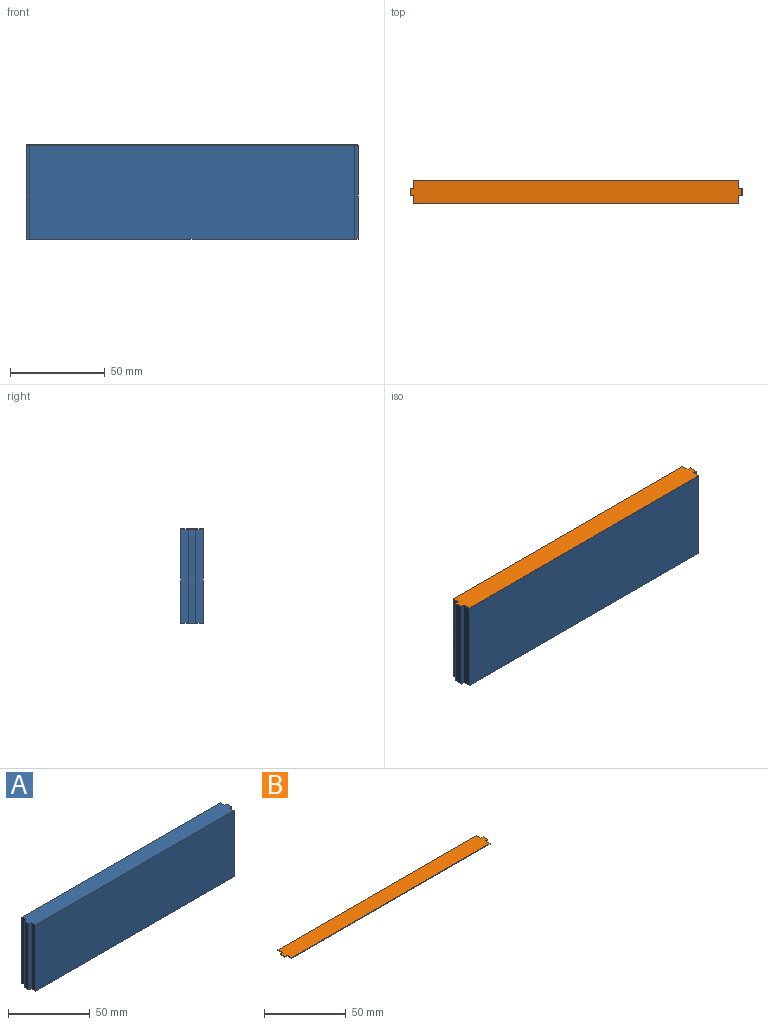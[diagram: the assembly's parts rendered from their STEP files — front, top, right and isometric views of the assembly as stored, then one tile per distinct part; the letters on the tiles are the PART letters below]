
ASSEMBLY  parts=2 mates=1
PART A: 14 faces, bbox 175x12x49.5 mm
  f0: plane 49.5x4mm, normal (-1,0,0), area 198mm2, adj f3,f4,f5,f8
  f1: plane 49.5x4mm, normal (-1,0,0), area 198mm2, adj f3,f5,f7,f8
  f2: plane 49.5x4mm, normal (-1,0,0), area 198mm2, adj f4,f5,f6,f8
  f3: plane 49.5x2mm, normal (0,1,0), area 99mm2, adj f0,f1,f5,f8
  f4: plane 49.5x2mm, normal (0,-1,0), area 99mm2, adj f0,f2,f5,f8
  f5: plane 175x12mm, normal (0,0,-1), area 2068mm2, adj f0,f1,f2,f3,f4,f6,f7,f9
  f6: plane 171x49.5mm, normal (0,-1,0), area 8464.5mm2, adj f2,f5,f8,f13
  f7: plane 171x49.5mm, normal (0,1,0), area 8464.5mm2, adj f1,f5,f8,f12
  f8: plane 175x12mm, normal (0,0,1), area 2068mm2, adj f0,f1,f2,f3,f4,f6,f7,f9
  f9: plane 49.5x2mm, normal (0,1,0), area 99mm2, adj f5,f8,f11,f12
  f10: plane 49.5x2mm, normal (0,-1,0), area 99mm2, adj f5,f8,f11,f13
  f11: plane 49.5x4mm, normal (1,0,0), area 198mm2, adj f5,f8,f9,f10
  f12: plane 49.5x4mm, normal (1,0,0), area 198mm2, adj f5,f7,f8,f9
  f13: plane 49.5x4mm, normal (1,0,0), area 198mm2, adj f5,f6,f8,f10
PART B: 14 faces, bbox 175x12x0.5 mm
  f0: plane 4x0.5mm, normal (-1,0,0), area 2mm2, adj f3,f4,f5,f8
  f1: plane 4x0.5mm, normal (-1,0,0), area 2mm2, adj f3,f5,f7,f8
  f2: plane 4x0.5mm, normal (-1,0,0), area 2mm2, adj f4,f5,f6,f8
  f3: plane 2x0.5mm, normal (0,1,0), area 1mm2, adj f0,f1,f5,f8
  f4: plane 2x0.5mm, normal (0,-1,0), area 1mm2, adj f0,f2,f5,f8
  f5: plane 175x12mm, normal (0,0,-1), area 2068mm2, adj f0,f1,f2,f3,f4,f6,f7,f9
  f6: plane 171x0.5mm, normal (0,-1,0), area 85.5mm2, adj f2,f5,f8,f13
  f7: plane 171x0.5mm, normal (0,1,0), area 85.5mm2, adj f1,f5,f8,f12
  f8: plane 175x12mm, normal (0,0,1), area 2068mm2, adj f0,f1,f2,f3,f4,f6,f7,f9
  f9: plane 2x0.5mm, normal (0,-1,0), area 1mm2, adj f5,f8,f11,f13
  f10: plane 2x0.5mm, normal (0,1,0), area 1mm2, adj f5,f8,f11,f12
  f11: plane 4x0.5mm, normal (1,0,0), area 2mm2, adj f5,f8,f9,f10
  f12: plane 4x0.5mm, normal (1,0,0), area 2mm2, adj f5,f7,f8,f10
  f13: plane 4x0.5mm, normal (1,0,0), area 2mm2, adj f5,f6,f8,f9
PLACE A t=(-17.48,63.18,-30.52)mm
PLACE B t=(-17.48,63.18,18.98)mm
MATE planar A.f8 <-> B.f5  axis (0,0,1) through (68.02,57.18,18.98)mm
